# Revit family: xxxxFaucet-Lavatory-Grohe-Essence-23485_Series
name_source: partatom
category: Plumbing Fixtures
units: mm (PartAtom-declared; Revit-internal decimal feet)

## family parameters
Always vertical = No
Cut with Voids When Loaded = No
OmniClass Number = 23.45.55.14
OmniClass Title = Single Faucets
Part Type = Normal
Room Calculation Point = No
Round Connector Dimension = Use Diameter
Shared = Yes
Work Plane-Based = Yes

## types (5) — shared parameters
ADA Compliant = Yes
ASME A112.18.1/CSA B125.1 = Yes
Assembly Code = D2020300
CW Connection = No
CWFU = 1.5
Compliance Certifications = Lead Plumbing Laws & NSF 61
Default Elevation = 0"
Description = Single Hole Single-Handle M-Size Bathroom Faucet 1.2 GPM
EPA WaterSense® Certified = Yes
Energy Policy Act of 1992 = Yes
Flow Rate = 1.2 gpm (4.5 L/min)
HW Connection = No
HWFU = 1.5
Height = 7 5/8"
Height- Spout = 6 5/16"
ICC/ANSI A117.1 = Yes
Installation Instruction Link = https://americanstandard.box.com
Installation Type = Deck-Mounted
Length = 4 1/2"
Manufacturer = Grohe
Max. Hot Water Temp. = 158 °F
Min Max. Operating Pressure = 7.25 psi - 145 psi
Overall Length = 6 1/8"
Price = Prices may vary. Please consult Manufacturer Representative for most up-to-date price list.
Product Page URL = https://americanstandard.box.com
Revised Date = 03/02/2022
Tempered Water Connection = Yes
Tempered Water Connection Diameter = 3/8"
URL = https://www.grohe.us
US Federal and State material regulations = Yes
Vent Connection = No
WFU = 2
Warranty Documentation Link = https://cdn.cloud.grohe.com
Waste Connection = No
cUPC Compliant = Yes

## per-type parameters (varying)
| type | Finish | Material |
| 2348500A | Brass-Grohe-00A-StarLight Chrome | Brass-Grohe-00A-StarLight Chrome |
| 23485GNA | Brass-Grohe-GNA-Brushed Cool Sunset | Brass-Grohe-GNA-Brushed Cool Sunset |
| 23485A0A | Brass-Grohe-A0A-Hard Graphite | Brass-Grohe-A0A-Hard Graphite |
| 23485BEA | Brass-Grohe-BEA-Polished Nickel Infinity Finish | Brass-Grohe-BEA-Polished Nickel Infinity Finish |
| 23485ENA | Brass-Grohe-ENA-Brushed Nickel Infinity Finish | Brass-Grohe-ENA-Brushed Nickel Infinity Finish |

note: column(s) folded — value = type name in every type: Model

## geometry (parser evidence)
native form markers: Sweep x2
no freeform markers — native parametric forms only
